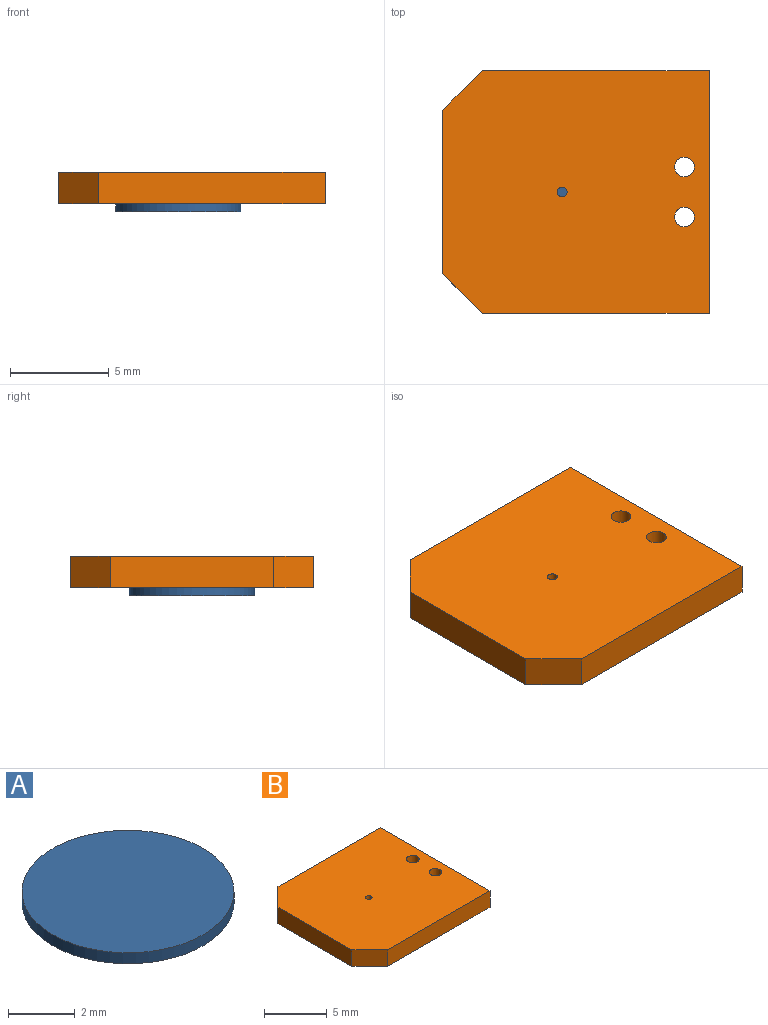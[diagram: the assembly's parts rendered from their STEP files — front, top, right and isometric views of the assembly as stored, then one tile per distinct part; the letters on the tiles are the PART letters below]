
ASSEMBLY  parts=2 mates=1
PART A: 3 faces, bbox 6.4x6.4x0.4 mm
  f0: cylinder r=3.17mm len=6.35mm, axis (0,0,1), area 8mm2, adj f1,f2
  f1: plane 6.35x6.35mm, normal (0,0,-1), area 31.7mm2, adj f0
  f2: plane 6.35x6.35mm, normal (0,0,1), area 31.7mm2, adj f0
PART B: 11 faces, bbox 13.5x12.3x1.6 mm
  f0: plane 13.5x12.3mm, normal (0,0,1), area 160.3mm2, adj f2,f3,f4,f5,f6,f7,f8,f9
  f1: plane 13.5x12.3mm, normal (0,0,-1), area 160.3mm2, adj f2,f3,f4,f5,f6,f7,f8,f9
  f2: plane 12.3x1.6mm, normal (1,0,0), area 19.7mm2, adj f0,f1,f3,f5
  f3: plane 11.5x1.6mm, normal (0,1,0), area 18.4mm2, adj f0,f1,f2,f10
  f4: plane 8.3x1.6mm, normal (-1,0,0), area 13.3mm2, adj f0,f1,f9,f10
  f5: plane 11.5x1.6mm, normal (0,-1,0), area 18.4mm2, adj f0,f1,f2,f9
  f6: cylinder r=0.25mm len=1.6mm, axis (0,0,1), area 2.5mm2, adj f0,f1
  f7: cylinder r=0.5mm len=1.6mm, axis (0,0,1), area 5mm2, adj f0,f1
  f8: cylinder r=0.5mm len=1.6mm, axis (0,0,1), area 5mm2, adj f0,f1
  f9: plane 2x2mm, normal (-0.71,-0.71,0), area 4.5mm2, adj f0,f1,f4,f5
  f10: plane 2x2mm, normal (-0.71,0.71,0), area 4.5mm2, adj f0,f1,f3,f4
PLACE A at identity
PLACE B at identity fixed
MATE fastened A.f0 <-> B.f6  axis (0,0,1) through (0,0,0)mm
